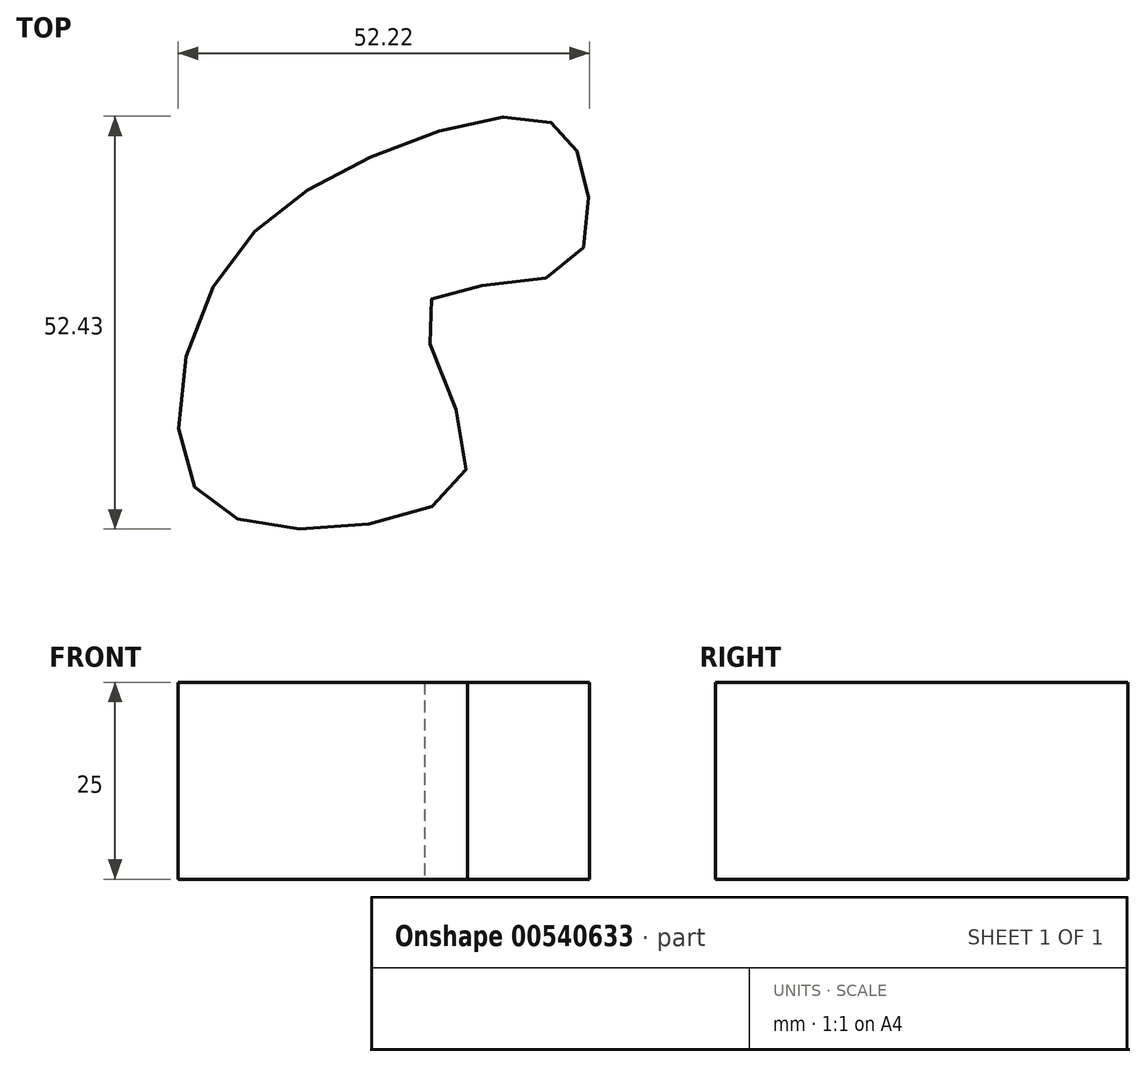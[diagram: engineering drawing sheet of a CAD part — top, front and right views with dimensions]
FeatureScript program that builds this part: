
annotation { "Feature Type Name" : "Feature", "Feature Type Description" : "" }
export const myFeature = defineFeature(function(context is Context, id is Id, definition is map)
    precondition{}
    {
        {
            var Q0;
            Q0=qCreatedBy(makeId("Top.planeOp"),FACE);
            var sketch = newSketch(context, id + "F0", { "sketchPlane" : qUnion([Q0])});
            skFitSpline(sketch, "E0", {"points": [v(-24.37, -2.3) * mm, v(-44.57, -19.1) * mm, v(-46.61, -44.3) * mm, v(-27.77, -49.3) * mm, v(-12.1, -41.13) * mm, v(-17.1, -20.92) * mm, v(0, -16.84) * mm, v(2.88, -4.8) * mm, v(-2.35, 2.46) * mm, v(-24.37, -2.3) * mm]});
            skSolve(sketch);
        }
        {
            var Q0;
            Q0=makeQuery(id+"F0.imprint","IMPRINT",FACE,{"disambiguationData":[TD([[makeQuery(id+"F0.imprint","IMPRINT",EDGE,{"derivedFrom":sQuery(id+"F0.wireOp",EDGE,"E0")}),1.0]])]});
            extrude(context, id + "F1", {"entities" : qUnion([Q0]), "depth" : 25 * mm, "offsetDistance" : 25 * mm});
        }
    });
